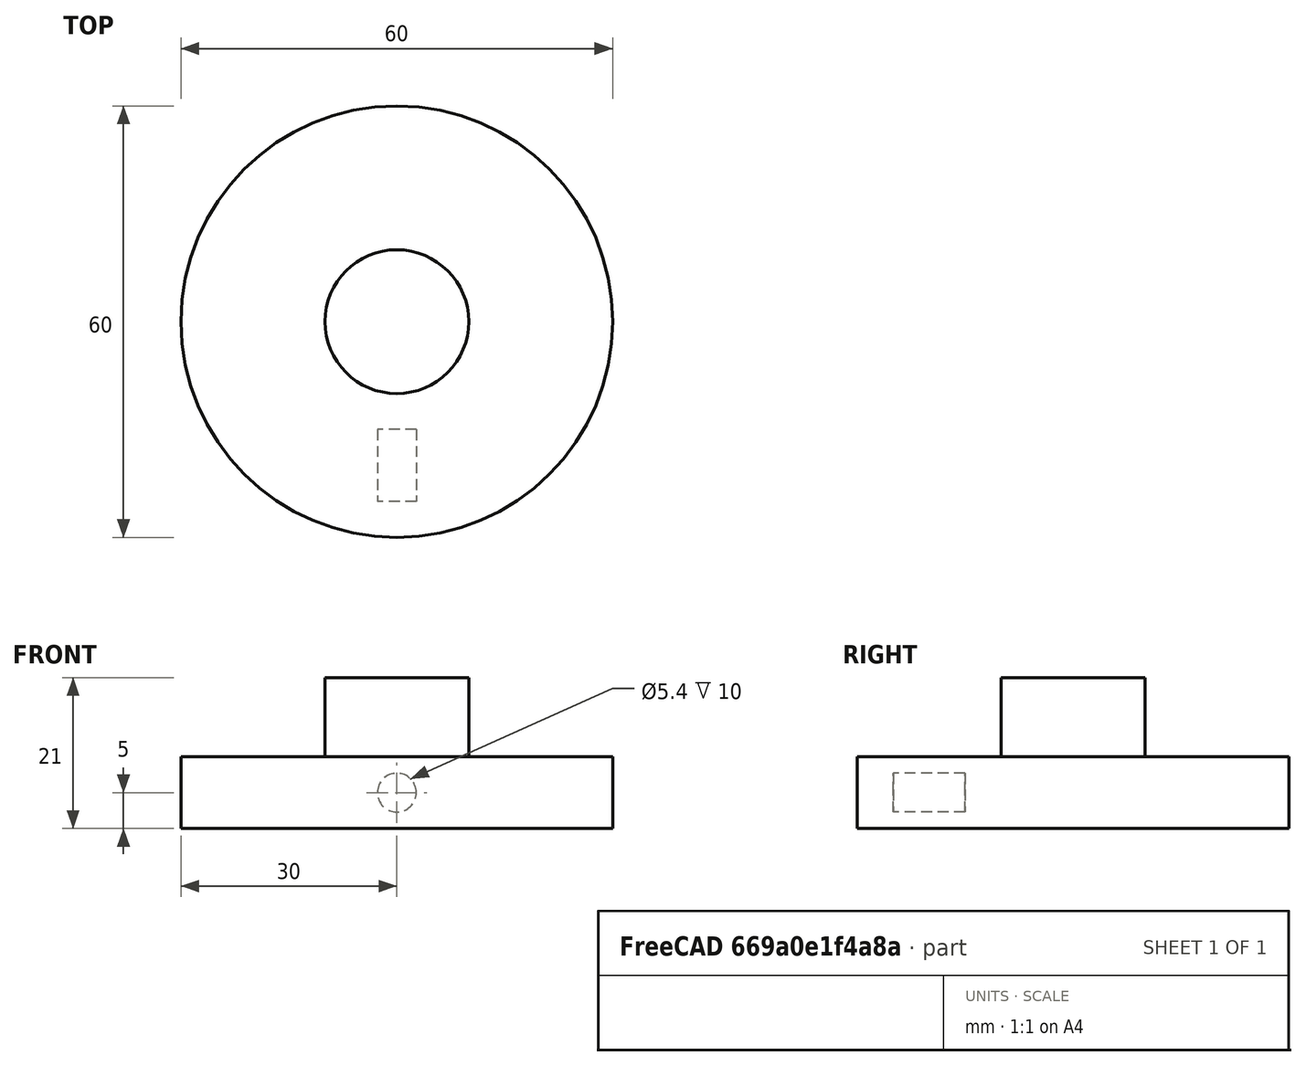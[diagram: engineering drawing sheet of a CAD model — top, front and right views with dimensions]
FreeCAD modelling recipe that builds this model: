
FCSTD DOCUMENT  (FreeCAD 0.16R6712 (Git))
Label: i-seasons2
License: All rights reserved
LicenseURL: http://en.wikipedia.org/wiki/All_rights_reserved
objects: Part::Cylinder×3, Part::MultiFuse×1, Part::Cut×1, Part::Feature×1
note: 6 computed .brp shape members not serialized (recipe doc carries the construction recipe); baked Part::Feature solids carry a one-line shape summary decoded from their .brp

FEATURE [Part::Cylinder] Cylinder  label="Cilindro"
  Angle = 360
  Height = 10
  Radius = 30
FEATURE [Part::Cylinder] Cylinder001  label="Cilindrotop"
  Angle = 360
  Height = 11
  Placement = pos=(0,0,10) rot=(0,0,1;0rad)
  Radius = 10
FEATURE [Part::Cylinder] Cylinder002  label="hole"
  Angle = 360
  Height = 10
  Placement = pos=(0,-15,5) rot=(1,0,0;1.5708rad)
  Radius = 2.7
FEATURE [Part::MultiFuse] Fusion
  Shapes = -> [Cylinder001,Cylinder]
FEATURE [Part::Cut] Cut  label="piece2"
  Base = -> Fusion
  Tool = -> Cylinder002
FEATURE [Part::Feature] Cut001  label="piece to print"
  shape: bbox 60 x 60 x 21 mm, 8 faces (baked)
